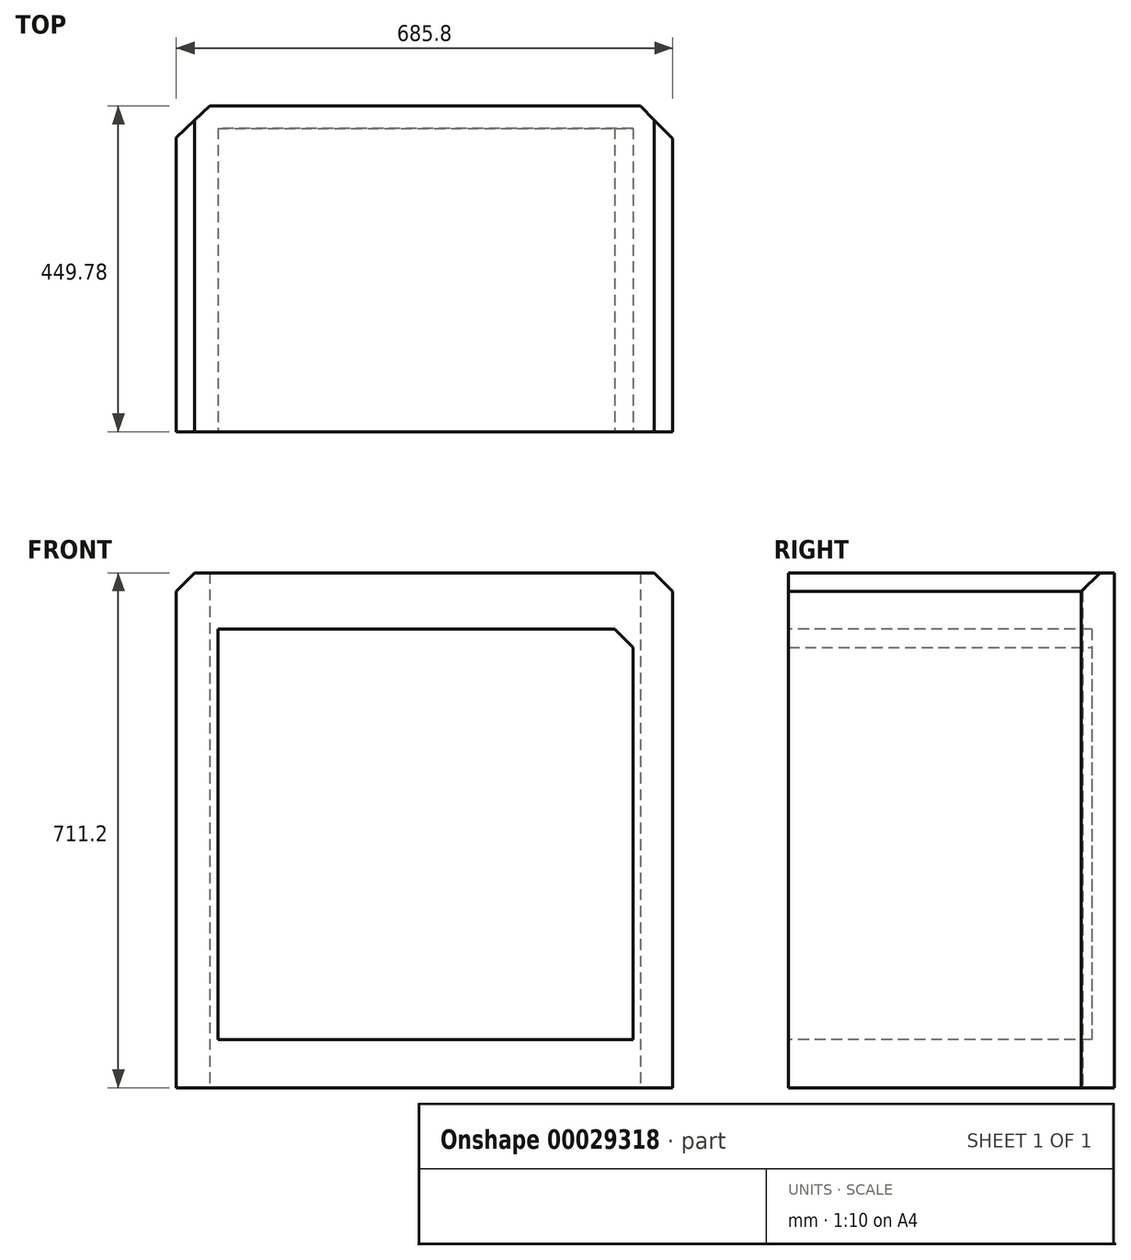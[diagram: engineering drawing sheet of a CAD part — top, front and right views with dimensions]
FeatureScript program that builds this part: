
annotation { "Feature Type Name" : "Feature", "Feature Type Description" : "" }
export const myFeature = defineFeature(function(context is Context, id is Id, definition is map)
    precondition{}
    {
        {
            var Q0;
            Q0=qCreatedBy(makeId("Top.planeOp"),FACE);
            var sketch = newSketch(context, id + "F0", { "sketchPlane" : qUnion([Q0])});
            skLineSegment(sketch, "E0.bottom", {"start": v(-10.94, -70.92) * mm, "end": v(583.99, -70.92) * mm});
            skLineSegment(sketch, "E0.top", {"start": v(-10.94, 449.78) * mm, "end": v(583.99, 449.78) * mm});
            skLineSegment(sketch, "E0.left", {"start": v(-57.28, -31.85) * mm, "end": v(-57.28, 406.36) * mm});
            skLineSegment(sketch, "E0.right", {"start": v(628.52, -31.85) * mm, "end": v(628.52, 404.51) * mm});
            skLineSegment(sketch, "E1", {"start": v(-10.94, 449.78) * mm, "end": v(-57.28, 406.36) * mm});
            skLineSegment(sketch, "E2", {"start": v(583.99, 449.78) * mm, "end": v(628.52, 404.51) * mm});
            skLineSegment(sketch, "E3", {"start": v(583.99, -70.92) * mm, "end": v(628.52, -31.85) * mm});
            skLineSegment(sketch, "E4", {"start": v(-57.28, -31.85) * mm, "end": v(-10.94, -70.92) * mm});
            skSolve(sketch);
        }
        {
            var Q0;
            Q0=makeQuery(id+"F0.imprint","IMPRINT",FACE,{"disambiguationData":[TD([[makeQuery(id+"F0.imprint","IMPRINT",EDGE,{"derivedFrom":sQuery(id+"F0.wireOp",EDGE,"E0.bottom")}),1.0]])]});
            extrude(context, id + "F1", {"entities" : qUnion([Q0]), "depth" : 711.2 * mm});
        }
        {
            var Q0;
            Q0=makeQuery(id+"F1.opExtrude","CAP_FACE",FACE,{"disambiguationData":[OSD([sQuery(id+"F0.wireOp",EDGE,"E0.bottom"),sQuery(id+"F0.wireOp",EDGE,"E0.top"),sQuery(id+"F0.wireOp",EDGE,"E0.left"),sQuery(id+"F0.wireOp",EDGE,"E0.right"),sQuery(id+"F0.wireOp",EDGE,"E1"),sQuery(id+"F0.wireOp",EDGE,"E2"),sQuery(id+"F0.wireOp",EDGE,"E3"),sQuery(id+"F0.wireOp",EDGE,"E4")])],"isStart":false});
            var sketch = newSketch(context, id + "F2", { "sketchPlane" : qUnion([Q0])});
            skLineSegment(sketch, "E5", {"start": v(-57.28, 0) * mm, "end": v(628.52, 0) * mm});
            skSolve(sketch);
        }
        {
            var Q0;
            {var subQ1=sQuery(id+"F2.wireOp",EDGE,"E5");Q0=makeQuery(id+"F2.imprint","IMPRINT",FACE,{"disambiguationData":[TD([[makeQuery(id+"F2.imprint","IMPRINT",EDGE,{"derivedFrom":subQ1}),-1.0]])]});}
            extrude(context, id + "F3", {"entities" : qUnion([Q0]), "operationType" : NewBodyOperationType.REMOVE, "oppositeDirection" : true, "depth" : 768.63 * mm});
        }
        {
            var Q0;
            Q0=makeQuery(id+"F3.boolean.opBoolean","COPY",FACE,{"derivedFrom":makeQuery(id+"F3.opExtrude","SWEPT_FACE",FACE,{"disambiguationData":[OSD([sQuery(id+"F2.wireOp",EDGE,"E5")])]})});
            var sketch = newSketch(context, id + "F4", { "sketchPlane" : qUnion([Q0])});
            skLineSegment(sketch, "E6", {"start": v(0, 633.2) * mm, "end": v(628.52, 633.2) * mm});
            skLineSegment(sketch, "E7", {"start": v(573.74, 633.2) * mm, "end": v(573.74, 66.25) * mm});
            skLineSegment(sketch, "E8", {"start": v(573.74, 66.25) * mm, "end": v(0, 66.25) * mm});
            skLineSegment(sketch, "E9", {"start": v(0, 633.2) * mm, "end": v(0, 66.25) * mm});
            skSolve(sketch);
        }
        {
            var Q0;
            {var subQ1=sQuery(id+"F4.wireOp",EDGE,"E7");Q0=makeQuery(id+"F4.imprint","IMPRINT",FACE,{"disambiguationData":[TD([[makeQuery(id+"F4.imprint","IMPRINT",EDGE,{"derivedFrom":subQ1}),-1.0]])]});}
            extrude(context, id + "F5", {"entities" : qUnion([Q0]), "operationType" : NewBodyOperationType.REMOVE, "oppositeDirection" : true, "depth" : 419.1 * mm});
        }
        {
            var Q0;
            Q0=makeQuery(id+"F1.opExtrude","CAP_EDGE",EDGE,{"disambiguationData":[OSD([sQuery(id+"F0.wireOp",EDGE,"E0.right")])],"isStart":false});
            var Q1;
            Q1=makeQuery(id+"F5.boolean.opBoolean","COPY",EDGE,{"derivedFrom":makeQuery(id+"F5.opExtrude","SWEPT_EDGE",EDGE,{"disambiguationData":[OSD([sQuery(id+"F4.wireOp",EDGE,"E6"),sQuery(id+"F4.wireOp",EDGE,"E7")])]})});
            chamfer(context, id + "F6", {"entities" : qUnion([Q0, Q1]), "width" : 25.4 * mm, "tangentPropagation" : true});
        }
        {
            var Q0;
            Q0=makeQuery(id+"F1.opExtrude","CAP_EDGE",EDGE,{"disambiguationData":[OSD([sQuery(id+"F0.wireOp",EDGE,"E0.left")])],"isStart":false});
            chamfer(context, id + "F7", {"entities" : qUnion([Q0]), "width" : 25.4 * mm, "tangentPropagation" : true});
        }
    });
